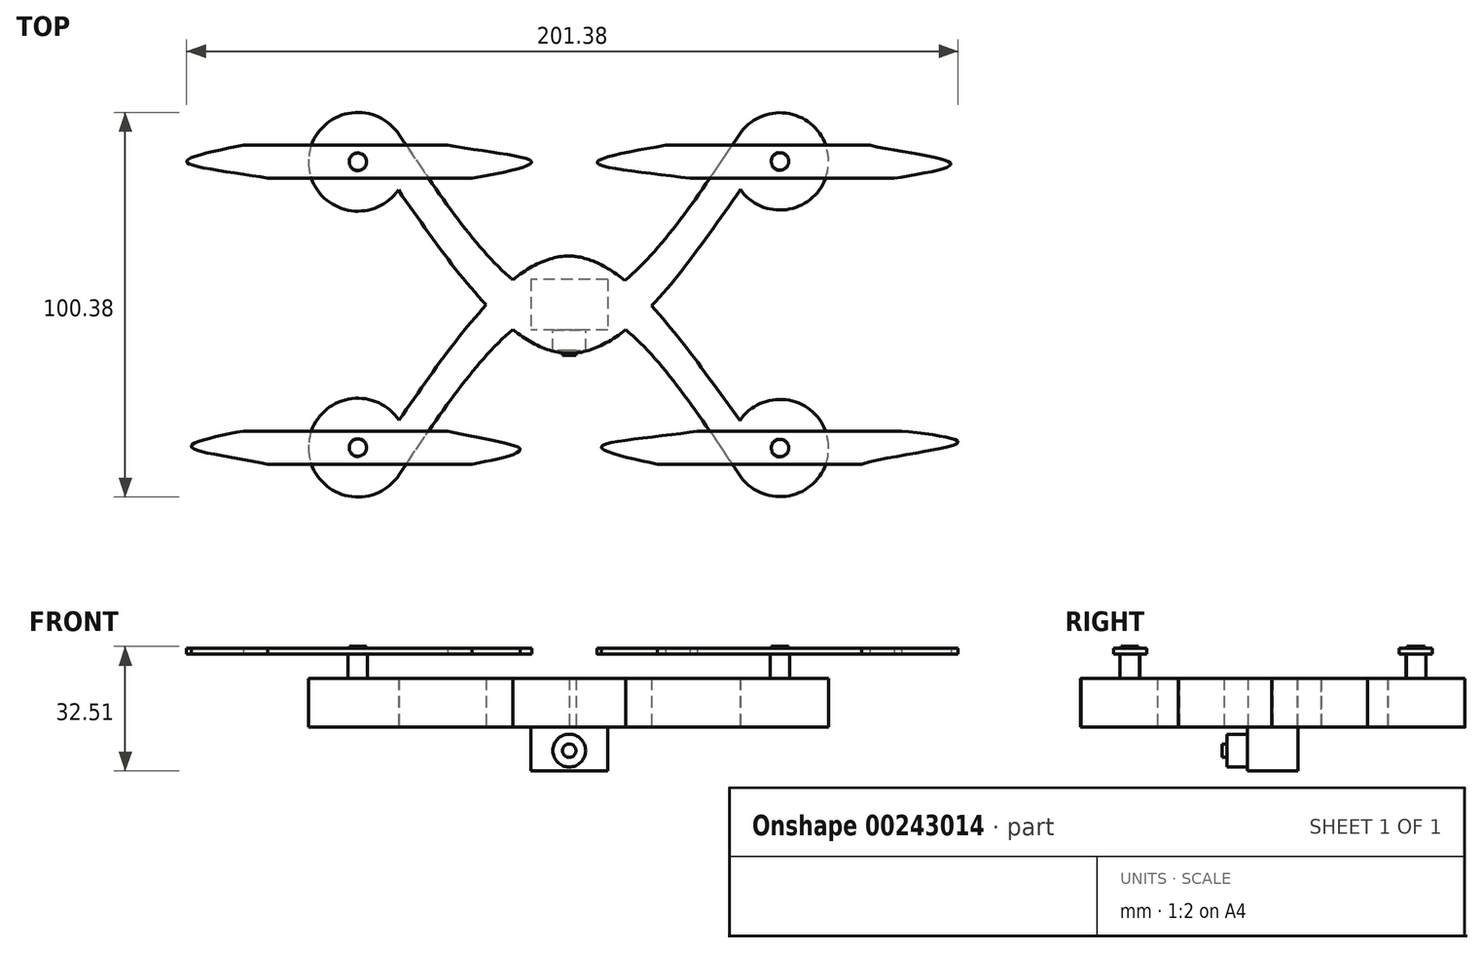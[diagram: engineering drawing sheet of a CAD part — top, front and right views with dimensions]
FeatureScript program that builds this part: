
annotation { "Feature Type Name" : "Feature", "Feature Type Description" : "" }
export const myFeature = defineFeature(function(context is Context, id is Id, definition is map)
    precondition{}
    {
        {
            var Q0;
            Q0=qCreatedBy(makeId("Top.planeOp"),FACE);
            var sketch = newSketch(context, id + "F0", { "sketchPlane" : qUnion([Q0])});
            skPoint(sketch, "E0.middle", {"position": v(0, 0) * mm});
            skFitSpline(sketch, "E1", {"points": [v(-44.45, 44.45) * mm, v(0, 0) * mm, v(44.45, 44.45) * mm], "startDerivative": vector(88.9, -133.35) * mm, "endDerivative": vector(88.9, 133.35) * mm});
            skCircle(sketch, "E2", {"center": v(0, 0) * mm, "radius": 12.7 * mm});
            skFitSpline(sketch, "E3", {"points": [v(-44.45, -44.45) * mm, v(0, 0) * mm, v(44.45, -44.45) * mm], "startDerivative": vector(88.9, 133.35) * mm, "endDerivative": vector(88.9, -133.35) * mm});
            skFitSpline(sketch, "E4", {"points": [v(-44.61, 29.91) * mm, v(0, -12.7) * mm, v(44.66, 30.05) * mm], "startDerivative": vector(89.07, -127.4) * mm, "endDerivative": vector(88.73, 128.21) * mm});
            skFitSpline(sketch, "E5", {"points": [v(-44.45, -30.15) * mm, v(0, 12.7) * mm, v(44.58, -30.18) * mm], "startDerivative": vector(87.95, 126.91) * mm, "endDerivative": vector(89.85, -122.43) * mm});
            skArc(sketch, "E6", {"start": v(-44.45, -44.45) * mm, "mid": v(-68.06, -37.3) * mm, "end": v(-44.45, -30.15) * mm});
            skArc(sketch, "E7", {"start": v(-44.45, 44.45) * mm, "mid": v(-68.06, 37.45) * mm, "end": v(-44.61, 29.91) * mm});
            skArc(sketch, "E8", {"start": v(44.66, 30.05) * mm, "mid": v(67.72, 37.6) * mm, "end": v(44.45, 44.45) * mm});
            skArc(sketch, "E9", {"start": v(44.45, -44.45) * mm, "mid": v(67.72, -37.52) * mm, "end": v(44.58, -30.18) * mm});
            skSolve(sketch);
        }
        {
            var Q0;
            Q0 = qSketchRegion(id + "F0", true);
            var Q1;
            {var subQ0=sQuery(id+"F0.wireOp",EDGE,"E2");var subQ1=sQuery(id+"F0.wireOp",EDGE,"E1");var subQ2=makeQuery(id+"F0.imprint","INTERSECT",VERTEX,{"disambiguationData":[OD(0.0)],"derivedFrom":[subQ1,subQ0]});Q1=makeQuery(id+"F0.imprint","IMPRINT",FACE,{"disambiguationData":[TD([[makeQuery(id+"F0.imprint","IMPRINT",EDGE,{"disambiguationData":[TD([[subQ2,-1.0]])],"derivedFrom":subQ1}),-1.0]])]});}
            var Q2;
            {var subQ0=sQuery(id+"F0.wireOp",EDGE,"E3");var subQ1=sQuery(id+"F0.wireOp",EDGE,"E1");var subQ2=makeQuery(id+"F0.imprint","INTERSECT",VERTEX,{"derivedFrom":[subQ1,subQ0]});Q2=makeQuery(id+"F0.imprint","IMPRINT",FACE,{"disambiguationData":[TD([[makeQuery(id+"F0.imprint","IMPRINT",EDGE,{"disambiguationData":[TD([[subQ2,-1.0]])],"derivedFrom":subQ1}),-1.0]])]});}
            extrude(context, id + "F1", {"entities" : qUnion([Q0, Q1, Q2]), "depth" : 12.7 * mm});
        }
        {
            var Q0;
            Q0=makeQuery(id+"F1.opExtrude","CAP_FACE",FACE,{"disambiguationData":[OSD([sQuery(id+"F0.wireOp",EDGE,"E1"),sQuery(id+"F0.wireOp",EDGE,"E2"),sQuery(id+"F0.wireOp",EDGE,"E3"),sQuery(id+"F0.wireOp",EDGE,"E4"),sQuery(id+"F0.wireOp",EDGE,"E5"),sQuery(id+"F0.wireOp",EDGE,"E6"),sQuery(id+"F0.wireOp",EDGE,"E7"),sQuery(id+"F0.wireOp",EDGE,"E8"),sQuery(id+"F0.wireOp",EDGE,"E9")])],"isStart":false});
            var sketch = newSketch(context, id + "F2", { "sketchPlane" : qUnion([Q0])});
            skCircle(sketch, "E10", {"center": v(-55.17, -37.3) * mm, "radius": 2.54 * mm});
            skCircle(sketch, "E11", {"center": v(-55.17, 37.3) * mm, "radius": 2.54 * mm});
            skCircle(sketch, "E12", {"center": v(55.02, 37.4) * mm, "radius": 2.54 * mm});
            skCircle(sketch, "E13", {"center": v(55.02, -37.4) * mm, "radius": 2.54 * mm});
            skSolve(sketch);
        }
        {
            var Q0;
            Q0=makeQuery(id+"F2.imprint","IMPRINT",FACE,{"disambiguationData":[TD([[makeQuery(id+"F2.imprint","IMPRINT",EDGE,{"derivedFrom":sQuery(id+"F2.wireOp",EDGE,"E10")}),1.0]])]});
            var Q1;
            Q1=makeQuery(id+"F2.imprint","IMPRINT",FACE,{"disambiguationData":[TD([[makeQuery(id+"F2.imprint","IMPRINT",EDGE,{"derivedFrom":sQuery(id+"F2.wireOp",EDGE,"E13")}),1.0]])]});
            var Q2;
            Q2=makeQuery(id+"F2.imprint","IMPRINT",FACE,{"disambiguationData":[TD([[makeQuery(id+"F2.imprint","IMPRINT",EDGE,{"derivedFrom":sQuery(id+"F2.wireOp",EDGE,"E12")}),1.0]])]});
            var Q3;
            Q3=makeQuery(id+"F2.imprint","IMPRINT",FACE,{"disambiguationData":[TD([[makeQuery(id+"F2.imprint","IMPRINT",EDGE,{"derivedFrom":sQuery(id+"F2.wireOp",EDGE,"E11")}),1.0]])]});
            extrude(context, id + "F3", {"entities" : qUnion([Q0, Q1, Q2, Q3]), "operationType" : NewBodyOperationType.ADD, "depth" : 6.35 * mm});
        }
        {
            var Q0;
            Q0=makeQuery(id+"F3.opExtrude","CAP_FACE",FACE,{"disambiguationData":[OSD([sQuery(id+"F2.wireOp",EDGE,"E11")])],"isStart":false});
            var sketch = newSketch(context, id + "F4", { "sketchPlane" : qUnion([Q0])});
            skLineSegment(sketch, "E14.bottom", {"start": v(-25.33, 32.98) * mm, "end": v(-78.67, 32.98) * mm});
            skLineSegment(sketch, "E14.top", {"start": v(-31.68, 41.62) * mm, "end": v(-85.02, 41.62) * mm});
            skPoint(sketch, "E14.middle", {"position": v(-55.17, 37.3) * mm});
            skLineSegment(sketch, "E15.bottom", {"start": v(78.45, 41.62) * mm, "end": v(25.11, 41.62) * mm});
            skLineSegment(sketch, "E15.top", {"start": v(84.8, 32.98) * mm, "end": v(31.46, 32.98) * mm});
            skPoint(sketch, "E15.middle", {"position": v(54.96, 37.3) * mm});
            skLineSegment(sketch, "E16.bottom", {"start": v(-25.33, -41.6) * mm, "end": v(-78.67, -41.6) * mm});
            skLineSegment(sketch, "E16.top", {"start": v(-31.68, -32.97) * mm, "end": v(-85.02, -32.97) * mm});
            skPoint(sketch, "E16.middle", {"position": v(-55.17, -37.3) * mm});
            skLineSegment(sketch, "E17.bottom", {"start": v(86.71, -32.97) * mm, "end": v(33.37, -32.97) * mm});
            skLineSegment(sketch, "E17.top", {"start": v(76.32, -41.6) * mm, "end": v(22.98, -41.6) * mm});
            skPoint(sketch, "E17.middle", {"position": v(54.85, -37.3) * mm});
            skPoint(sketch, "E17.cornerSnap0", {"position": v(-58.35, -32.97) * mm});
            skFitSpline(sketch, "E18", {"points": [v(-85.02, 41.62) * mm, v(-99.86, 37.3) * mm, v(-78.67, 32.98) * mm], "startDerivative": vector(-44.53, -8.66) * mm, "endDerivative": vector(44.53, -8.61) * mm});
            skFitSpline(sketch, "E19", {"points": [v(-31.68, 41.62) * mm, v(-9.8, 37.3) * mm, v(-25.33, 32.98) * mm], "startDerivative": vector(46.57, -8.66) * mm, "endDerivative": vector(-46.57, -8.61) * mm});
            skFitSpline(sketch, "E20", {"points": [v(31.46, 32.98) * mm, v(7.28, 37.06) * mm, v(25.11, 41.62) * mm], "startDerivative": vector(-53.52, 7.94) * mm, "endDerivative": vector(53.47, 9.33) * mm});
            skFitSpline(sketch, "E21", {"points": [v(84.8, 32.98) * mm, v(99.64, 36.83) * mm, v(78.45, 41.62) * mm], "startDerivative": vector(44.6, 7.28) * mm, "endDerivative": vector(-44.46, 10) * mm});
            skFitSpline(sketch, "E22", {"points": [v(-78.67, -41.6) * mm, v(-98.7, -37.06) * mm, v(-85.02, -32.97) * mm], "startDerivative": vector(-41.03, 9.3) * mm, "endDerivative": vector(41.1, 7.97) * mm});
            skFitSpline(sketch, "E23", {"points": [v(-25.33, -41.6) * mm, v(-12.8, -37.75) * mm, v(-31.68, -32.97) * mm], "startDerivative": vector(37.63, 7.32) * mm, "endDerivative": vector(-37.5, 9.95) * mm});
            skFitSpline(sketch, "E24", {"points": [v(33.37, -32.97) * mm, v(8.43, -37.06) * mm, v(22.98, -41.6) * mm], "startDerivative": vector(-43.67, -7.97) * mm, "endDerivative": vector(43.61, -9.3) * mm});
            skFitSpline(sketch, "E25", {"points": [v(86.71, -32.97) * mm, v(101.5, -35.9) * mm, v(76.32, -41.6) * mm], "startDerivative": vector(44.53, -4.62) * mm, "endDerivative": vector(-44.16, -12.61) * mm});
            skSolve(sketch);
        }
        {
            var Q0;
            Q0 = qSketchRegion(id + "F4", true);
            extrude(context, id + "F5", {"entities" : qUnion([Q0]), "operationType" : NewBodyOperationType.ADD, "depth" : 1.52 * mm});
        }
        {
            var Q0;
            Q0=makeQuery(id+"F1.opExtrude","CAP_FACE",FACE,{"disambiguationData":[OSD([sQuery(id+"F0.wireOp",EDGE,"E1"),sQuery(id+"F0.wireOp",EDGE,"E2"),sQuery(id+"F0.wireOp",EDGE,"E3"),sQuery(id+"F0.wireOp",EDGE,"E4"),sQuery(id+"F0.wireOp",EDGE,"E5"),sQuery(id+"F0.wireOp",EDGE,"E6"),sQuery(id+"F0.wireOp",EDGE,"E7"),sQuery(id+"F0.wireOp",EDGE,"E8"),sQuery(id+"F0.wireOp",EDGE,"E9")])],"isStart":true});
            var sketch = newSketch(context, id + "F6", { "sketchPlane" : qUnion([Q0])});
            skLineSegment(sketch, "E26.bottom", {"start": v(10.05, -6.58) * mm, "end": v(-10.05, -6.58) * mm});
            skLineSegment(sketch, "E26.top", {"start": v(10.05, 6.58) * mm, "end": v(-10.05, 6.58) * mm});
            skLineSegment(sketch, "E26.left", {"start": v(10.05, -6.58) * mm, "end": v(10.05, 6.58) * mm});
            skLineSegment(sketch, "E26.right", {"start": v(-10.05, -6.58) * mm, "end": v(-10.05, 6.58) * mm});
            skPoint(sketch, "E26.middle", {"position": v(0, 0) * mm});
            skSolve(sketch);
        }
        {
            var Q0;
            Q0 = qSketchRegion(id + "F6", true);
            extrude(context, id + "F7", {"entities" : qUnion([Q0]), "operationType" : NewBodyOperationType.ADD, "depth" : 11.43 * mm});
        }
        {
            var Q0;
            Q0=makeQuery(id+"F7.opExtrude","SWEPT_FACE",FACE,{"disambiguationData":[OSD([sQuery(id+"F6.wireOp",EDGE,"E26.top")])]});
            var sketch = newSketch(context, id + "F8", { "sketchPlane" : qUnion([Q0])});
            skCircle(sketch, "E27", {"center": v(0, -6.12) * mm, "radius": 4.29 * mm});
            skSolve(sketch);
        }
        {
            var Q0;
            Q0 = qSketchRegion(id + "F8", true);
            extrude(context, id + "F9", {"entities" : qUnion([Q0]), "operationType" : NewBodyOperationType.ADD, "depth" : 5.33 * mm});
        }
        {
            var Q0;
            Q0=makeQuery(id+"F9.opExtrude","CAP_FACE",FACE,{"disambiguationData":[OSD([sQuery(id+"F8.wireOp",EDGE,"E27")])],"isStart":false});
            var sketch = newSketch(context, id + "F10", { "sketchPlane" : qUnion([Q0])});
            skCircle(sketch, "E28", {"center": v(0, -6.12) * mm, "radius": 1.75 * mm});
            skSolve(sketch);
        }
        {
            var Q0;
            Q0=makeQuery(id+"F10.imprint","IMPRINT",FACE,{"disambiguationData":[TD([[makeQuery(id+"F10.imprint","IMPRINT",EDGE,{"derivedFrom":sQuery(id+"F10.wireOp",EDGE,"E28")}),1.0]])]});
            extrude(context, id + "F11", {"entities" : qUnion([Q0]), "operationType" : NewBodyOperationType.ADD, "depth" : 1.27 * mm});
        }
        {
            var Q0;
            Q0=makeQuery(id+"F1.opExtrude","CAP_FACE",FACE,{"disambiguationData":[OSD([sQuery(id+"F0.wireOp",EDGE,"E1"),sQuery(id+"F0.wireOp",EDGE,"E2"),sQuery(id+"F0.wireOp",EDGE,"E3"),sQuery(id+"F0.wireOp",EDGE,"E4"),sQuery(id+"F0.wireOp",EDGE,"E5"),sQuery(id+"F0.wireOp",EDGE,"E6"),sQuery(id+"F0.wireOp",EDGE,"E7"),sQuery(id+"F0.wireOp",EDGE,"E8"),sQuery(id+"F0.wireOp",EDGE,"E9")])],"isStart":false});
            var sketch = newSketch(context, id + "F12", { "sketchPlane" : qUnion([Q0])});
            skCircle(sketch, "E29", {"center": v(-55.17, 37.3) * mm, "radius": 2.27 * mm});
            skCircle(sketch, "E30", {"center": v(-55.17, -37.3) * mm, "radius": 2.27 * mm});
            skCircle(sketch, "E31", {"center": v(55.02, 37.4) * mm, "radius": 2.27 * mm});
            skCircle(sketch, "E32", {"center": v(55.02, -37.4) * mm, "radius": 2.27 * mm});
            skSolve(sketch);
        }
        {
            var Q0;
            Q0 = qSketchRegion(id + "F12", true);
            extrude(context, id + "F13", {"entities" : qUnion([Q0]), "operationType" : NewBodyOperationType.ADD, "depth" : 8.38 * mm});
        }
    });
